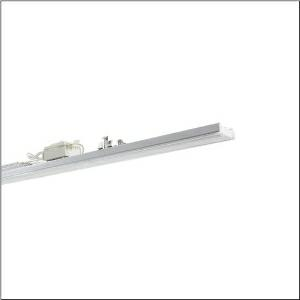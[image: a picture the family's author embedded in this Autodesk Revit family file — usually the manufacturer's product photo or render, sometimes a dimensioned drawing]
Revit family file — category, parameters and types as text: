
# Revit family: licross_r__11_recessed_mo_51te10cn49xg_a378
name_source: partatom
category: Lighting Fixtures
units: mm (PartAtom-declared; Revit-internal decimal feet)

## family parameters
Cut with Voids When Loaded = No
Host = Face
Light Source = No
Part Type = Normal
Room Calculation Point = No
Round Connector Dimension = Use Diameter
Shared = No

## types (1)
- --- (1 x LED, 9050 lm, 49.3 W, 4000K)
    Apparent Load = 49 VA
    CIE Flux Codes = 50 81 96 100 100
    Color Rendering = 80
    Color Temperature = 4000K
    Default Elevation = 1800 mm
    Description = Licross® 11 Recessed MO, luminaire insert, of sheet steel, galvanised, coil coated, white, length: 1.500mm, width: 66mm, height: 67mm, LED rated luminous flux: 9.050lm, light colour: 840, control gear: ON/OFF Multilumen, CLOi, with plug, 3-pole, with phase selection, mains connection: 220..240V, AC, 50/60Hz, start of lifetime: 49W, end of service life: 55W, internal wiring halogen-free, primary optical cover: cover, of PMMA, light emission: direct distribution, primary light characteristic: symmetric, protection rating (complete): IP54, insulation class (complete): insulation class I (protective earthing), certification: CE, ENEC, VDE, UKCA, protection symbol: D if used in an environment with non-conductive dust loads with corresponding accessories, impact resistance: IK06, permissible ambient temperature for indoor applications: -35..+40°C, corresponds to IFS (International Featured Standards) requirements for safety and quality in the food industry, reducing of maximum allowable ambient temperature of 5°C with ceiling mounting, LABS conformity tested according to VDMA 24364:2018-05, packaging unit: 1 piece
    Height = 58 mm
    Lamp = 1 x LED
    Lamp Light Flux = 9050 lm
    Lamp Power = 49.3 W
    Lamp count = 1
    Length = 1500 mm
    Luminous efficacy = 184 lm/W
    Manufacturer = Siteco
    ModVariant = No
    Model = 51TE10CN49XG
    Mounting Place = Ceiling
    Mounting Type = Pendant
    Number of Poles = 1
    OnlyDefault = Yes
    Power Factor = 1
    Product Name = Licross® 11 Recessed MO
    Product group = luminaire insert | ceiling pendant
    ProductGroupID = 902
    Protection Class = Protection class I
    Protection Degree = IP 54
    RLX_Detail_Level = 1
    RLX_Emergency_Light_Flux = 0 lm
    RLX_Emergency_Type = 0
    RLX_Emergency_Type_DB = No
    RlxData = <blob elided: 22217 chars, md5=72a0c572>
    Socket = socket
    Standby Power = 0 W
    System Light Flux = 9050 lm
    System Power = 49 W
    Type Comments = factory setting: luminous flux: 100 % | (A | C | E) | 113 mA
    Type Image = l_1296930.jpg
    URL = http://relux.com
    VarID = @adj_106655
    Voltage = 0 V
    Weight = 0.00 kg
    Width = 66 mm

## geometry (parser evidence)
native form markers: Blend x4, Sweep x10
no freeform markers — native parametric forms only
